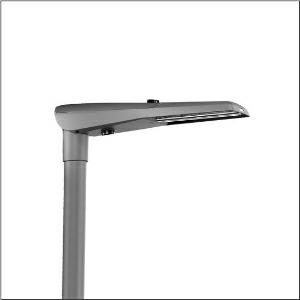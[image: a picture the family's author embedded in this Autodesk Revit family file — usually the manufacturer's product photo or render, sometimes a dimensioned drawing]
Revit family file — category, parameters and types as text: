
# Revit family: streetlight_sl_11_iq_mini___st1_2a_5xc2ac1y08he_5079
name_source: partatom
category: Lighting Fixtures
units: mm (PartAtom-declared; Revit-internal decimal feet)

## family parameters
Cut with Voids When Loaded = No
Host = Face
Light Source = No
Part Type = Normal
Room Calculation Point = No
Round Connector Dimension = Use Diameter
Shared = No

## types (1)
- --- (1 x LED, 6820 lm, 63.2 W, 2200K)
    Apparent Load = 63 VA
    CIE Flux Codes = 32 70 96 100 100
    Color Rendering = 70
    Color Temperature = 2200K
    Default Elevation = 1800 mm
    Description = Streetlight SL 11 iQ mini, mast luminaire, primary light control with 3 zone facetted reflector, of plastic, silver coated, highly specular, primary optical cover: cover, of PMMA, transparent, light distribution: ST1.2a, light emission: direct distribution, primary light characteristic: asymmetric, installation type: post-top, side-entry, lamps: LED, High Power LED, rated values: 8.070lm | 59,6W | 135,4lm/W (begin service life); end service life: 8.070lm | 62,8W; at 50% lumin. flux: 4.035lm | 28,3W | 142,6lm/W, colour temperature: 2200/2700/3000/4000K, colour rendering: CRI > 70, light colour: 722/727/730/740, light setting 1 begin service life: 100% | 8.070lm | 59,6W | 135,4lm/W | 3.000K, light setting 1 end service life: 62,8W, further light settings possible, control: pre-setting: logarithmic dimming characteristic, Street-Remote, Auto-Match, Temp-Guard, Lumen-Switch, Night-Set, Smart-Wire, Light-Fading, Desk-Remote (wireless, voltage-free reading and setting of iQ features in the workshop via application-optimized NFC function/RFID function), optimised constant luminous flux control (CLO 2.0), with cable H07RN-F 3x 1.5mm², mains connection: 230..240V, AC, 50/60Hz, connection cable pre-assembled, cable length: 8,5m, luminaire housing, of diecast aluminium, powder-coated, SITECO metallic grey (DB 702S), please order mast flange separately, inclination adjustable without tools: 0°, 5°, 10°, 15° (post-top) | 0°, -5°, -10°, -15° (side-entry), sealing non-destructively replaceable, multi-level sealing system, length: 736mm, width: 174mm, height: 116mm, mast flange for spigot size: 42mm (side-entry): 5XC10008XM4, 60/48mm (side-entry/post-top): 5XC10108XM2, 76/60mm (side-entry/post-top): 5XC10108XM1, equipment: Power, Smart Interface below and above, protection rating (complete): IP66, insulation class (complete): insulation class II (safety insulation), certification: CE, ENEC, ENEC+, VDE, UKCA, impact resistance: IK10, permissible operating ambient temperature for outdoor applications: -25..+50°C, standard-compliant lighting for roads and squares, Environmental Product Declaration (EPD) tested and certified by an independent institute, packaging unit: 1 piece

Light Distribution: ST1.2a
    Height = 116 mm
    Lamp = 1 x LED
    Lamp Light Flux = 6820 lm
    Lamp Power = 63.2 W
    Lamp count = 1
    Length = 736 mm
    Luminous efficacy = 108 lm/W
    Manufacturer = Siteco
    ModVariant = No
    Model = 5XC2AC1Y08HE
    Number of Poles = 1
    OnlyDefault = Yes
    Power Factor = 1
    Product Name = Streetlight SL 11 iQ mini | ST1.2a
    Product group = mast luminaire | pylon top
    ProductGroupID = 6100
    Protection Class = Protection class II
    Protection Degree = IP 66
    RLX_Detail_Level = 1
    RLX_Emergency_Light_Flux = 0 lm
    RLX_Emergency_Type = 0
    RLX_Emergency_Type_DB = No
    RlxData = <blob elided: 53865 chars, md5=98c6872a>
    Socket = socket
    Standby Power = 0 W
    System Light Flux = 6820 lm
    System Power = 63 W
    Type Comments = individual setting: luminous flux: 100 % | dim-lin: 254 | 866 mA
    Type Image = l_1006751.jpg
    URL = http://relux.com
    VarID = @adj_041599
    Voltage = 0 V
    Weight = 0.00 kg
    Width = 174 mm

## geometry (parser evidence)
native form markers: Blend x4, Sweep x11
no freeform markers — native parametric forms only
